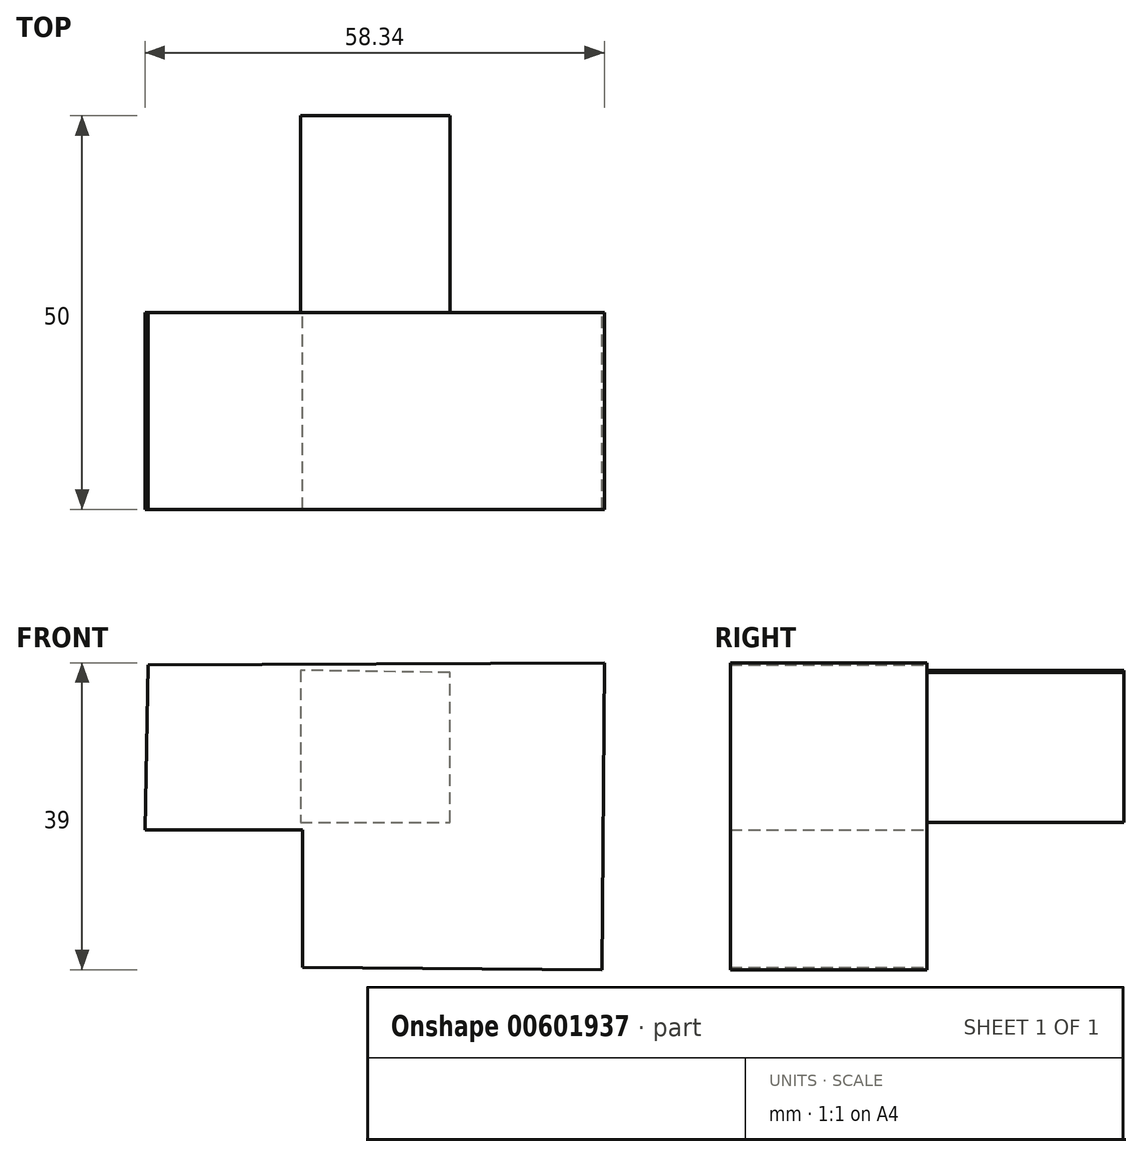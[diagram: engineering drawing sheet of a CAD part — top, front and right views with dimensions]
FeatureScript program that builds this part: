
annotation { "Feature Type Name" : "Feature", "Feature Type Description" : "" }
export const myFeature = defineFeature(function(context is Context, id is Id, definition is map)
    precondition{}
    {
        {
            var Q0;
            Q0=qCreatedBy(makeId("Front.planeOp"),FACE);
            var sketch = newSketch(context, id + "F0", { "sketchPlane" : qUnion([Q0])});
            skLineSegment(sketch, "E0", {"start": v(-57.66, 29.48) * mm, "end": v(-58, 8.48) * mm});
            skLineSegment(sketch, "E1", {"start": v(-58, 8.48) * mm, "end": v(-38, 8.48) * mm});
            skLineSegment(sketch, "E2", {"start": v(-38, 8.48) * mm, "end": v(-38, -8.92) * mm});
            skLineSegment(sketch, "E3", {"start": v(-38, -8.92) * mm, "end": v(0, -9.26) * mm});
            skLineSegment(sketch, "E4", {"start": v(0, -9.26) * mm, "end": v(0.34, 29.74) * mm});
            skLineSegment(sketch, "E5", {"start": v(0.34, 29.74) * mm, "end": v(-57.66, 29.48) * mm});
            skSolve(sketch);
        }
        {
            var Q0;
            Q0 = qSketchRegion(id + "F0", true);
            extrude(context, id + "F1", {"entities" : qUnion([Q0]), "depth" : 25 * mm, "offsetDistance" : 25 * mm});
        }
        {
            var Q0;
            Q0=qCreatedBy(makeId("Front.planeOp"),FACE);
            var sketch = newSketch(context, id + "F2", { "sketchPlane" : qUnion([Q0])});
            skLineSegment(sketch, "E6", {"start": v(-38.27, 28.8) * mm, "end": v(-38.27, 9.48) * mm});
            skLineSegment(sketch, "E7", {"start": v(-38.27, 9.48) * mm, "end": v(-19.28, 9.48) * mm});
            skLineSegment(sketch, "E8", {"start": v(-19.28, 9.48) * mm, "end": v(-19.28, 28.48) * mm});
            skLineSegment(sketch, "E9", {"start": v(-19.28, 28.48) * mm, "end": v(-38.27, 28.8) * mm});
            skSolve(sketch);
        }
        {
            var Q0;
            Q0 = qSketchRegion(id + "F2", true);
            extrude(context, id + "F3", {"entities" : qUnion([Q0]), "operationType" : NewBodyOperationType.ADD, "oppositeDirection" : true, "depth" : 25 * mm, "offsetDistance" : 25 * mm});
        }
    });
